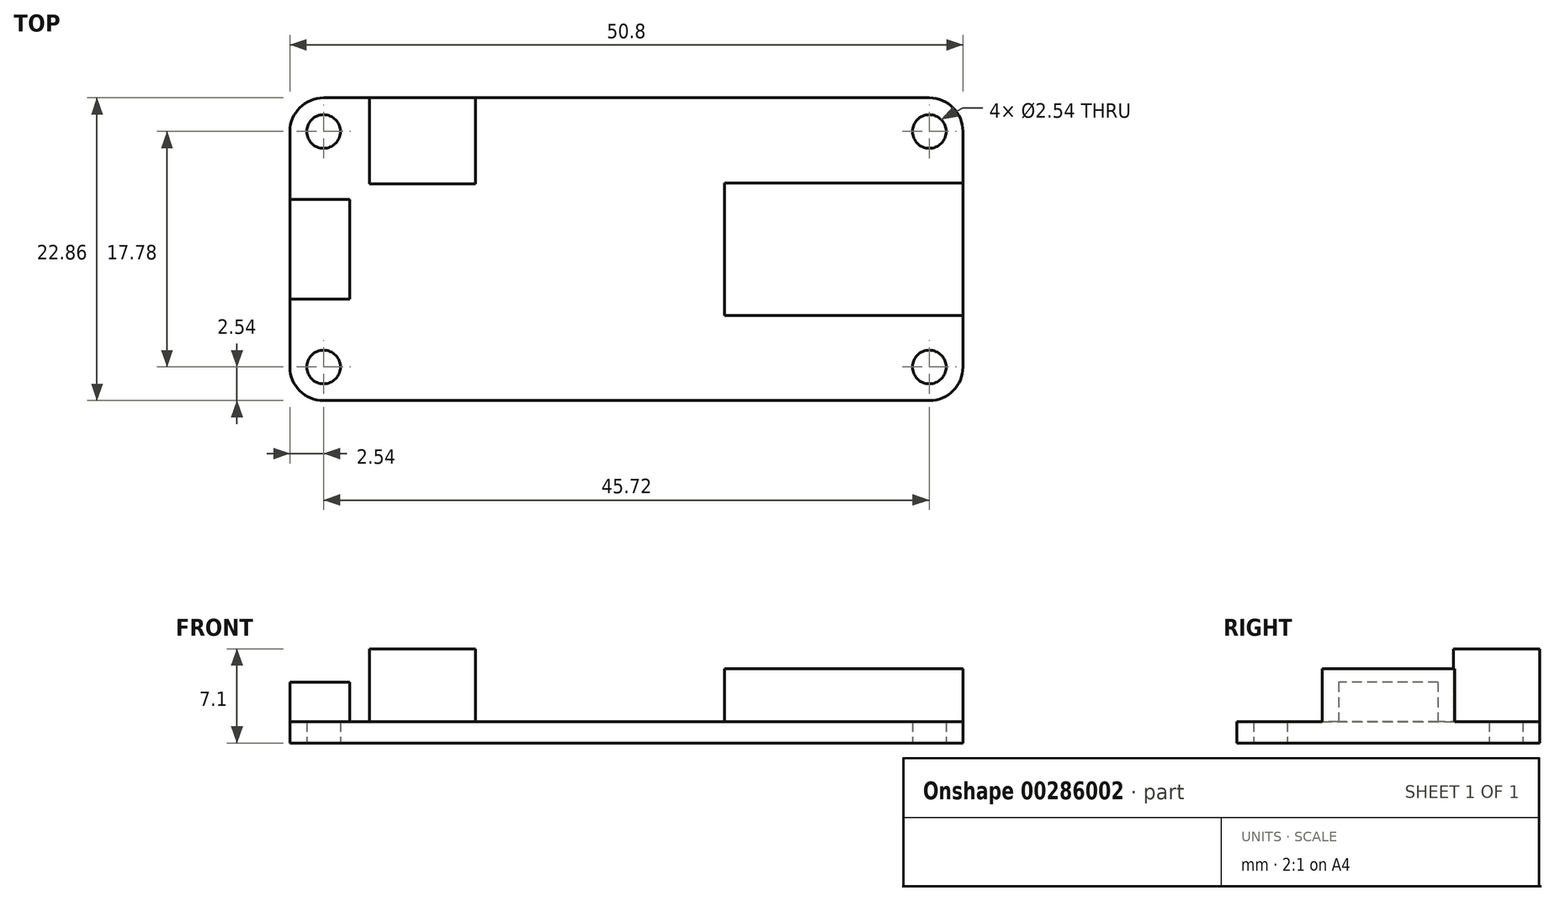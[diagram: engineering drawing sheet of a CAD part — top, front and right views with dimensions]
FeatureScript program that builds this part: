
annotation { "Feature Type Name" : "Feature", "Feature Type Description" : "" }
export const myFeature = defineFeature(function(context is Context, id is Id, definition is map)
    precondition{}
    {
        {
            var Q0;
            Q0=qCreatedBy(makeId("Top.planeOp"),FACE);
            var sketch = newSketch(context, id + "F0", { "sketchPlane" : qUnion([Q0])});
            skLineSegment(sketch, "E0.bottom", {"start": v(22.86, 11.43) * mm, "end": v(-22.86, 11.43) * mm});
            skLineSegment(sketch, "E0.top", {"start": v(22.86, -11.43) * mm, "end": v(-22.86, -11.43) * mm});
            skLineSegment(sketch, "E0.left", {"start": v(25.4, 8.9) * mm, "end": v(25.4, -8.9) * mm});
            skLineSegment(sketch, "E0.right", {"start": v(-25.4, 8.9) * mm, "end": v(-25.4, -8.9) * mm});
            skPoint(sketch, "E0.middle", {"position": v(0, 0) * mm});
            skCircle(sketch, "E1", {"center": v(-22.86, 8.89) * mm, "radius": 1.27 * mm});
            skCircle(sketch, "E2", {"center": v(22.86, 8.89) * mm, "radius": 1.27 * mm});
            skCircle(sketch, "E3", {"center": v(-22.86, -8.89) * mm, "radius": 1.27 * mm});
            skCircle(sketch, "E4", {"center": v(22.86, -8.89) * mm, "radius": 1.27 * mm});
            skPoint(sketch, "E5.visualSharp", {"position": v(-25.4, 11.43) * mm});
            skArc(sketch, "E5.filletArc", {"start": v(-22.86, 11.43) * mm, "mid": v(-24.66, 10.69) * mm, "end": v(-25.4, 8.9) * mm});
            skPoint(sketch, "E6.visualSharp", {"position": v(-25.4, -11.43) * mm});
            skArc(sketch, "E6.filletArc", {"start": v(-25.4, -8.9) * mm, "mid": v(-24.66, -10.69) * mm, "end": v(-22.86, -11.43) * mm});
            skPoint(sketch, "E7.visualSharp", {"position": v(25.4, -11.43) * mm});
            skArc(sketch, "E7.filletArc", {"start": v(22.86, -11.43) * mm, "mid": v(24.66, -10.69) * mm, "end": v(25.4, -8.9) * mm});
            skPoint(sketch, "E8.visualSharp", {"position": v(25.4, 11.43) * mm});
            skArc(sketch, "E8.filletArc", {"start": v(25.4, 8.9) * mm, "mid": v(24.66, 10.69) * mm, "end": v(22.86, 11.43) * mm});
            skSolve(sketch);
        }
        {
            var Q0;
            Q0=qSketchRegion(id+"F0",true);
            extrude(context, id + "F1", {"entities" : qUnion([Q0]), "depth" : 1.6 * mm});
        }
        {
            var Q0;
            Q0=makeQuery(id+"F1.opExtrude","CAP_FACE",FACE,{"disambiguationData":[OSD([sQuery(id+"F0.wireOp",EDGE,"E0.bottom"),sQuery(id+"F0.wireOp",EDGE,"E0.top"),sQuery(id+"F0.wireOp",EDGE,"E0.left"),sQuery(id+"F0.wireOp",EDGE,"E0.right"),sQuery(id+"F0.wireOp",EDGE,"E1"),sQuery(id+"F0.wireOp",EDGE,"E2"),sQuery(id+"F0.wireOp",EDGE,"E3"),sQuery(id+"F0.wireOp",EDGE,"E4"),sQuery(id+"F0.wireOp",EDGE,"E5.filletArc"),sQuery(id+"F0.wireOp",EDGE,"E6.filletArc"),sQuery(id+"F0.wireOp",EDGE,"E7.filletArc"),sQuery(id+"F0.wireOp",EDGE,"E8.filletArc")])],"isStart":false});
            var sketch = newSketch(context, id + "F2", { "sketchPlane" : qUnion([Q0])});
            skLineSegment(sketch, "E9.bottom", {"start": v(-25.4, 3.75) * mm, "end": v(-20.9, 3.75) * mm});
            skLineSegment(sketch, "E9.top", {"start": v(-25.4, -3.75) * mm, "end": v(-20.9, -3.75) * mm});
            skLineSegment(sketch, "E9.left", {"start": v(-25.4, 3.75) * mm, "end": v(-25.4, -3.75) * mm});
            skLineSegment(sketch, "E9.right", {"start": v(-20.9, 3.75) * mm, "end": v(-20.9, -3.75) * mm});
            skPoint(sketch, "E9.middle", {"position": v(-23.15, 0) * mm});
            skSolve(sketch);
        }
        {
            var Q0;
            Q0=qSketchRegion(id+"F2",true);
            extrude(context, id + "F3", {"entities" : qUnion([Q0]), "operationType" : NewBodyOperationType.ADD, "depth" : 3 * mm});
        }
        {
            var Q0;
            Q0=makeQuery(id+"F1.opExtrude","CAP_FACE",FACE,{"disambiguationData":[OSD([sQuery(id+"F0.wireOp",EDGE,"E0.bottom"),sQuery(id+"F0.wireOp",EDGE,"E0.top"),sQuery(id+"F0.wireOp",EDGE,"E0.left"),sQuery(id+"F0.wireOp",EDGE,"E0.right"),sQuery(id+"F0.wireOp",EDGE,"E1"),sQuery(id+"F0.wireOp",EDGE,"E2"),sQuery(id+"F0.wireOp",EDGE,"E3"),sQuery(id+"F0.wireOp",EDGE,"E4"),sQuery(id+"F0.wireOp",EDGE,"E5.filletArc"),sQuery(id+"F0.wireOp",EDGE,"E6.filletArc"),sQuery(id+"F0.wireOp",EDGE,"E7.filletArc"),sQuery(id+"F0.wireOp",EDGE,"E8.filletArc")])],"isStart":false});
            var sketch = newSketch(context, id + "F4", { "sketchPlane" : qUnion([Q0])});
            skLineSegment(sketch, "E10.bottom", {"start": v(25.4, -5) * mm, "end": v(7.4, -5) * mm});
            skLineSegment(sketch, "E10.top", {"start": v(25.4, 5) * mm, "end": v(7.4, 5) * mm});
            skLineSegment(sketch, "E10.left", {"start": v(25.4, -5) * mm, "end": v(25.4, 5) * mm});
            skLineSegment(sketch, "E10.right", {"start": v(7.4, -5) * mm, "end": v(7.4, 5) * mm});
            skPoint(sketch, "E10.middle", {"position": v(16.4, 0) * mm});
            skSolve(sketch);
        }
        {
            var Q0;
            Q0=makeQuery(id+"F4.imprint","IMPRINT",FACE,{"disambiguationData":[TD([[makeQuery(id+"F4.imprint","IMPRINT",EDGE,{"derivedFrom":sQuery(id+"F4.wireOp",EDGE,"E10.bottom")}),-1.0]])]});
            extrude(context, id + "F5", {"entities" : qUnion([Q0]), "operationType" : NewBodyOperationType.ADD, "depth" : 4 * mm});
        }
        {
            var Q0;
            Q0=makeQuery(id+"F1.opExtrude","CAP_FACE",FACE,{"disambiguationData":[OSD([sQuery(id+"F0.wireOp",EDGE,"E0.bottom"),sQuery(id+"F0.wireOp",EDGE,"E0.top"),sQuery(id+"F0.wireOp",EDGE,"E0.left"),sQuery(id+"F0.wireOp",EDGE,"E0.right"),sQuery(id+"F0.wireOp",EDGE,"E1"),sQuery(id+"F0.wireOp",EDGE,"E2"),sQuery(id+"F0.wireOp",EDGE,"E3"),sQuery(id+"F0.wireOp",EDGE,"E4"),sQuery(id+"F0.wireOp",EDGE,"E5.filletArc"),sQuery(id+"F0.wireOp",EDGE,"E6.filletArc"),sQuery(id+"F0.wireOp",EDGE,"E7.filletArc"),sQuery(id+"F0.wireOp",EDGE,"E8.filletArc")])],"isStart":false});
            var sketch = newSketch(context, id + "F6", { "sketchPlane" : qUnion([Q0])});
            skLineSegment(sketch, "E11.bottom", {"start": v(-19.4, 11.43) * mm, "end": v(-11.4, 11.43) * mm});
            skLineSegment(sketch, "E11.top", {"start": v(-19.4, 4.93) * mm, "end": v(-11.4, 4.93) * mm});
            skLineSegment(sketch, "E11.left", {"start": v(-19.4, 11.43) * mm, "end": v(-19.4, 4.93) * mm});
            skLineSegment(sketch, "E11.right", {"start": v(-11.4, 11.43) * mm, "end": v(-11.4, 4.93) * mm});
            skSolve(sketch);
        }
        {
            var Q0;
            Q0=makeQuery(id+"F6.imprint","IMPRINT",FACE,{"disambiguationData":[TD([[makeQuery(id+"F6.imprint","IMPRINT",EDGE,{"derivedFrom":sQuery(id+"F6.wireOp",EDGE,"E11.bottom")}),1.0]])]});
            extrude(context, id + "F7", {"entities" : qUnion([Q0]), "operationType" : NewBodyOperationType.ADD, "depth" : 5.5 * mm});
        }
    });
